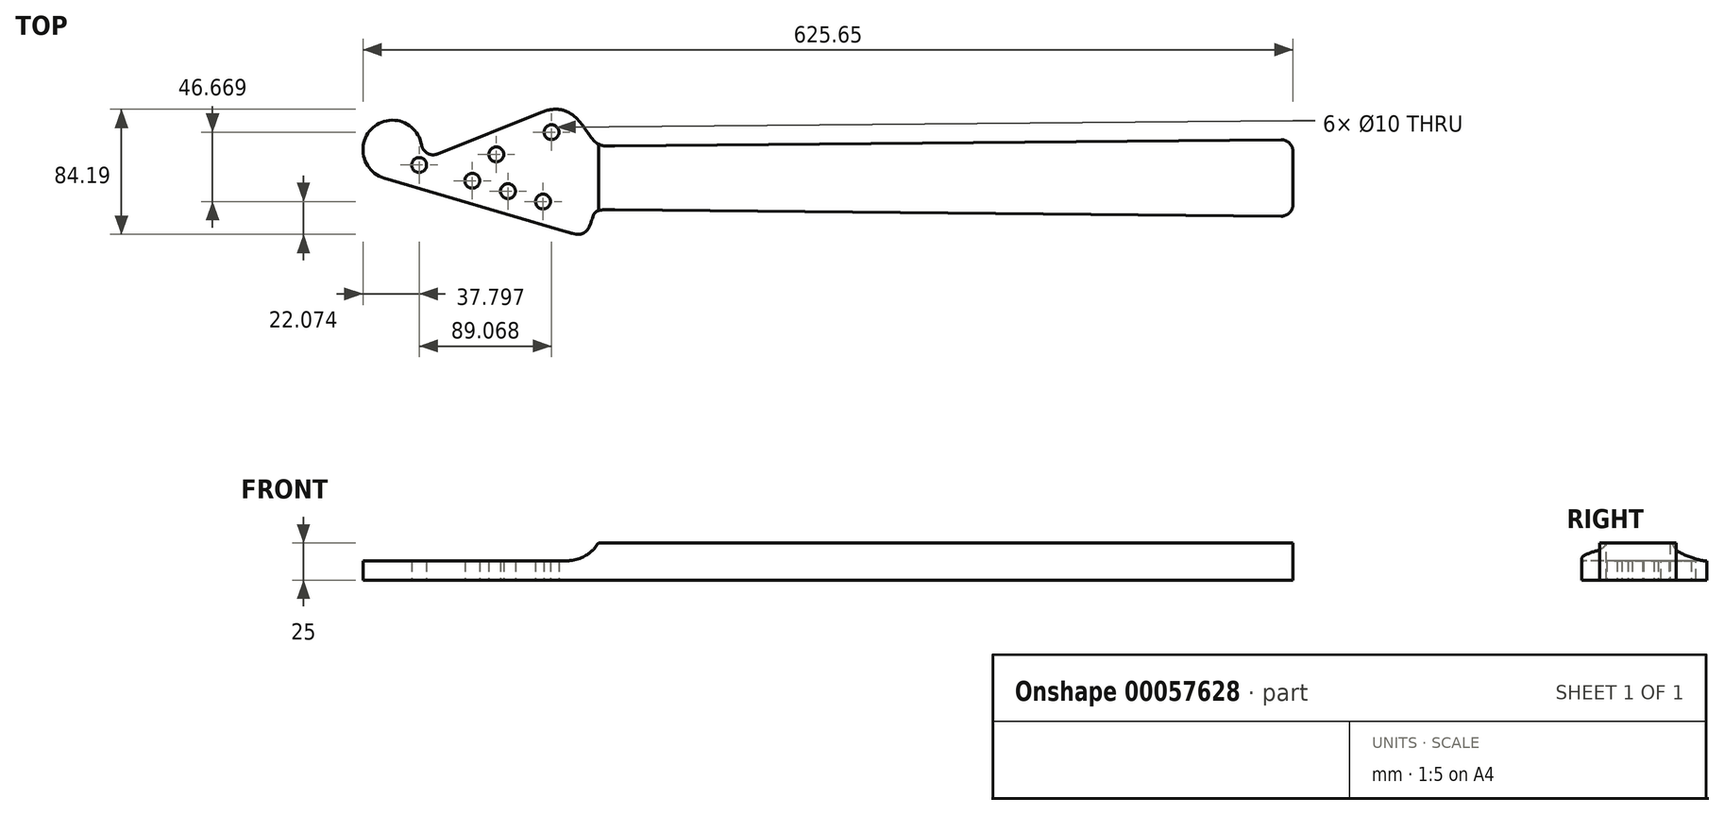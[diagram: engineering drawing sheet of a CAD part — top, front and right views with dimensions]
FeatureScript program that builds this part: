
annotation { "Feature Type Name" : "Feature", "Feature Type Description" : "" }
export const myFeature = defineFeature(function(context is Context, id is Id, definition is map)
    precondition{}
    {
        {
            var Q0;
            Q0=qCreatedBy(makeId("Top.planeOp"),FACE);
            var sketch = newSketch(context, id + "F0", { "sketchPlane" : qUnion([Q0])});
            skLineSegment(sketch, "E0", {"start": v(-545.56, 0) * mm, "end": v(270.45, 0) * mm, "construction": true});
            skLineSegment(sketch, "E1", {"start": v(-514.65, 21.5) * mm, "end": v(-514.65, -21.5) * mm, "construction": true});
            skText(sketch, "E2", { "text": "Nut", "fontName": "OpenSans-Regular.ttf"});
            skLineSegment(sketch, "E3", {"start": v(120.35, 27.5) * mm, "end": v(120.35, -27.5) * mm, "construction": true});
            skText(sketch, "E4", { "text": "Bridge\n", "fontName": "OpenSans-Regular.ttf"});
            skLineSegment(sketch, "E5", {"start": v(-514.65, 21.5) * mm, "end": v(120.35, 27.5) * mm, "construction": true});
            skLineSegment(sketch, "E6", {"start": v(-514.65, -21.5) * mm, "end": v(120.35, -27.5) * mm, "construction": true});
            skLineSegment(sketch, "E7", {"start": v(-514.65, 0) * mm, "end": v(120.35, 0) * mm});
            const initialGuessF0  = {"E2": [-0.53875, 0.11756, 1, 0, 0.01067], "E4": [0.1311, 0.11455, 1, 0, 0.02259]};
            skSetInitialGuess(sketch, initialGuessF0);
            skSolve(sketch);
        }
        {
            var Q0;
            Q0=qCreatedBy(makeId("Top.planeOp"),FACE);
            var sketch = newSketch(context, id + "F1", { "sketchPlane" : qUnion([Q0])});
            skLineSegment(sketch, "E8", {"start": v(-514.65, 21.5) * mm, "end": v(-514.65, -21.5) * mm});
            skSolve(sketch);
        }
        {
            var Q0;
            Q0=qCreatedBy(makeId("Top.planeOp"),FACE);
            var sketch = newSketch(context, id + "F2", { "sketchPlane" : qUnion([Q0])});
            skLineSegment(sketch, "E9", {"start": v(-479, 35.64) * mm, "end": v(-479, 0) * mm});
            skLineSegment(sketch, "E10", {"start": v(-514.65, 37.76) * mm, "end": v(120.35, 0) * mm, "construction": true});
            skLineSegment(sketch, "E11", {"start": v(120.35, 0) * mm, "end": v(-514.65, -21.5) * mm, "construction": true});
            skLineSegment(sketch, "E12", {"start": v(-514.65, 0) * mm, "end": v(-514.65, 37.76) * mm});
            skLineSegment(sketch, "E13", {"start": v(-514.65, 0) * mm, "end": v(-479, 0) * mm});
            skLineSegment(sketch, "E14", {"start": v(-445.37, 33.64) * mm, "end": v(-445.37, 0) * mm});
            skLineSegment(sketch, "E15", {"start": v(-445.37, 0) * mm, "end": v(-479, 0) * mm});
            skLineSegment(sketch, "E16", {"start": v(-445.37, 0) * mm, "end": v(-413.62, 0) * mm});
            skLineSegment(sketch, "E17", {"start": v(-413.62, 0) * mm, "end": v(-413.62, 31.75) * mm});
            skLineSegment(sketch, "E18", {"start": v(-413.62, 0) * mm, "end": v(-383.65, 0) * mm});
            skLineSegment(sketch, "E19", {"start": v(-383.65, 0) * mm, "end": v(-383.65, 29.97) * mm});
            skLineSegment(sketch, "E20", {"start": v(-383.65, 0) * mm, "end": v(-355.36, 0) * mm});
            skLineSegment(sketch, "E21", {"start": v(-355.36, 0) * mm, "end": v(-355.36, 28.29) * mm});
            skLineSegment(sketch, "E22", {"start": v(-355.36, 0) * mm, "end": v(-328.66, 0) * mm});
            skLineSegment(sketch, "E23", {"start": v(-328.66, 0) * mm, "end": v(-328.66, 26.7) * mm});
            skLineSegment(sketch, "E24", {"start": v(-328.66, 0) * mm, "end": v(-303.46, 0) * mm});
            skLineSegment(sketch, "E25", {"start": v(-303.46, 0) * mm, "end": v(-303.46, 25.2) * mm});
            skLineSegment(sketch, "E26", {"start": v(-303.46, 0) * mm, "end": v(-279.67, 0) * mm});
            skLineSegment(sketch, "E27", {"start": v(-279.67, 0) * mm, "end": v(-279.67, 23.79) * mm});
            skLineSegment(sketch, "E28", {"start": v(-279.67, 0) * mm, "end": v(-257.22, 0) * mm});
            skLineSegment(sketch, "E29", {"start": v(-257.22, 0) * mm, "end": v(-257.22, 22.45) * mm});
            skLineSegment(sketch, "E30", {"start": v(-257.22, 0) * mm, "end": v(-236.03, 0) * mm});
            skLineSegment(sketch, "E31", {"start": v(-236.03, 0) * mm, "end": v(-236.03, 21.2) * mm});
            skLineSegment(sketch, "E32", {"start": v(-236.03, 0) * mm, "end": v(-216.03, 0) * mm});
            skPoint(sketch, "E32.endSnap0", {"position": v(-246.63, 0) * mm});
            skLineSegment(sketch, "E33", {"start": v(-216.03, 0) * mm, "end": v(-216.03, 20) * mm});
            skLineSegment(sketch, "E34", {"start": v(-216.03, 0) * mm, "end": v(-197.15, 0) * mm});
            skLineSegment(sketch, "E35", {"start": v(-197.15, 0) * mm, "end": v(-197.15, 18.88) * mm});
            skLineSegment(sketch, "E36", {"start": v(-197.15, 0) * mm, "end": v(-179.33, 0) * mm});
            skLineSegment(sketch, "E37", {"start": v(-179.33, 0) * mm, "end": v(-179.33, 17.82) * mm});
            skLineSegment(sketch, "E38", {"start": v(-179.33, 0) * mm, "end": v(-162.5, 0) * mm});
            skLineSegment(sketch, "E39", {"start": v(-162.5, 0) * mm, "end": v(-162.5, 16.82) * mm});
            skLineSegment(sketch, "E40", {"start": v(-162.5, 0) * mm, "end": v(-146.63, 0) * mm});
            skLineSegment(sketch, "E41", {"start": v(-146.63, 0) * mm, "end": v(-146.63, 15.88) * mm});
            skLineSegment(sketch, "E42", {"start": v(-146.63, 0) * mm, "end": v(-131.65, 0) * mm});
            skLineSegment(sketch, "E43", {"start": v(-131.65, 0) * mm, "end": v(-131.65, 14.98) * mm});
            skLineSegment(sketch, "E44", {"start": v(-131.65, 0) * mm, "end": v(-117.5, 0) * mm});
            skLineSegment(sketch, "E45", {"start": v(-117.5, 0) * mm, "end": v(-117.5, 14.14) * mm});
            skLineSegment(sketch, "E46", {"start": v(-117.5, 0) * mm, "end": v(-104.16, 0) * mm});
            skLineSegment(sketch, "E47", {"start": v(-104.16, 0) * mm, "end": v(-104.16, 13.35) * mm});
            skLineSegment(sketch, "E48", {"start": v(-104.16, 0) * mm, "end": v(-91.56, 0) * mm});
            skLineSegment(sketch, "E49", {"start": v(-91.56, 0) * mm, "end": v(-91.56, 12.6) * mm});
            skLineSegment(sketch, "E50", {"start": v(-91.56, 0) * mm, "end": v(-79.66, 0) * mm});
            skLineSegment(sketch, "E51", {"start": v(-79.66, 0) * mm, "end": v(-79.66, 11.9) * mm});
            skLineSegment(sketch, "E52", {"start": v(-79.66, 0) * mm, "end": v(-68.44, 0) * mm});
            skLineSegment(sketch, "E53", {"start": v(-68.44, 0) * mm, "end": v(-68.44, 11.23) * mm});
            skSolve(sketch);
        }
        {
            var Q0;
            Q0=qCreatedBy(makeId("Top.planeOp"),FACE);
            var sketch = newSketch(context, id + "F3", { "sketchPlane" : qUnion([Q0])});
            skLineSegment(sketch, "E54", {"start": v(-514.65, 21.5) * mm, "end": v(-514.65, -21.5) * mm});
            skLineSegment(sketch, "E55", {"start": v(-514.65, -21.5) * mm, "end": v(-66.51, -25.73) * mm});
            skLineSegment(sketch, "E56", {"start": v(-58.44, -17.73) * mm, "end": v(-58.44, 17.73) * mm});
            skLineSegment(sketch, "E57", {"start": v(-66.51, 25.73) * mm, "end": v(-514.65, 21.5) * mm});
            skLineSegment(sketch, "E58", {"start": v(-68.44, 0) * mm, "end": v(-58.44, 0) * mm});
            skPoint(sketch, "E59.visualSharp", {"position": v(-58.44, -25.81) * mm});
            skArc(sketch, "E59.filletArc", {"start": v(-66.51, -25.73) * mm, "mid": v(-60.8, -23.42) * mm, "end": v(-58.44, -17.73) * mm});
            skPoint(sketch, "E60.visualSharp", {"position": v(-58.44, 25.81) * mm});
            skArc(sketch, "E60.filletArc", {"start": v(-58.44, 17.73) * mm, "mid": v(-60.8, 23.42) * mm, "end": v(-66.51, 25.73) * mm});
            skSolve(sketch);
        }
        {
            var Q0;
            Q0 = qSketchRegion(id + "F3", true);
            extrude(context, id + "F4", {"entities" : qUnion([Q0]), "depth" : 6 * mm});
        }
        {
            var Q0;
            Q0=makeQuery(id+"F4.opExtrude","CAP_FACE",FACE,{"disambiguationData":[OSD([sQuery(id+"F3.wireOp",EDGE,"E54"),sQuery(id+"F3.wireOp",EDGE,"E55"),sQuery(id+"F3.wireOp",EDGE,"E56"),sQuery(id+"F3.wireOp",EDGE,"E57")])],"isStart":false});
            cPlane(context, id + "F5", {"entities" : qUnion([Q0]), "cplaneType" : CPlaneType.OFFSET, "offset" : 0 * mm, "width" : 150 * mm, "height" : 150 * mm});
        }
        {
            var Q0;
            Q0=qCreatedBy(id+"F5.planeOp",FACE);
            var sketch = newSketch(context, id + "F6", { "sketchPlane" : qUnion([Q0])});
            skCircle(sketch, "E61", {"center": v(-429.5, 0) * mm, "radius": 3 * mm});
            skCircle(sketch, "E62", {"center": v(-369.5, 0) * mm, "radius": 3 * mm});
            skCircle(sketch, "E63", {"center": v(-316.06, 0) * mm, "radius": 3 * mm});
            skCircle(sketch, "E64", {"center": v(-268.45, 0) * mm, "radius": 3 * mm});
            skCircle(sketch, "E65", {"center": v(-226.03, 12.11) * mm, "radius": 3 * mm});
            skCircle(sketch, "E66", {"center": v(-226.03, -12.11) * mm, "radius": 3 * mm});
            skLineSegment(sketch, "E67", {"start": v(-226.03, 0) * mm, "end": v(-226.03, 12.11) * mm, "construction": true});
            skCircle(sketch, "E68", {"center": v(-170.92, 0) * mm, "radius": 3 * mm});
            skCircle(sketch, "E69", {"center": v(-139.14, 0) * mm, "radius": 3 * mm});
            skCircle(sketch, "E70", {"center": v(-110.83, 0) * mm, "radius": 3 * mm});
            skCircle(sketch, "E71", {"center": v(-85.6, 0) * mm, "radius": 3 * mm});
            skLineSegment(sketch, "E72.0", {"start": v(-514.65, 21.5) * mm, "end": v(120.35, 27.5) * mm});
            skLineSegment(sketch, "E73", {"start": v(-226.03, 0) * mm, "end": v(-226.03, 24.23) * mm, "construction": true});
            skSolve(sketch);
        }
        {
            var Q0;
            Q0 = qSketchRegion(id + "F6", true);
            var Q1;
            Q1=makeQuery(id+"F4.opExtrude","CAP_FACE",FACE,{"disambiguationData":[OSD([sQuery(id+"F3.wireOp",EDGE,"E54"),sQuery(id+"F3.wireOp",EDGE,"E55"),sQuery(id+"F3.wireOp",EDGE,"E56"),sQuery(id+"F3.wireOp",EDGE,"E57")])],"isStart":true});
            extrude(context, id + "F7", {"entities" : qUnion([Q0]), "operationType" : NewBodyOperationType.REMOVE, "oppositeDirection" : true, "endBoundEntityFace" : qUnion([Q1]), "depth" : 2 * mm});
        }
        {
            var Q0;
            Q0=makeQuery(id+"F4.opExtrude","SWEPT_FACE",FACE,{"disambiguationData":[OSD([sQuery(id+"F3.wireOp",EDGE,"E56")])]});
            var sketch = newSketch(context, id + "F8", { "sketchPlane" : qUnion([Q0])});
            skArc(sketch, "E74", {"start": v(53.48, 0) * mm, "mid": v(0, 6) * mm, "end": v(-53.48, 0) * mm});
            skLineSegment(sketch, "E75", {"start": v(-53.48, 0) * mm, "end": v(-53.48, 6) * mm});
            skLineSegment(sketch, "E76", {"start": v(-53.48, 6) * mm, "end": v(53.48, 6) * mm});
            skLineSegment(sketch, "E77", {"start": v(53.48, 6) * mm, "end": v(53.48, 0) * mm});
            skSolve(sketch);
        }
        {
            var Q0;
            Q0 = qSketchRegion(id + "F8", true);
            extrude(context, id + "F9", {"entities" : qUnion([Q0]), "operationType" : NewBodyOperationType.REMOVE, "endBound" : BoundingType.THROUGH_ALL, "oppositeDirection" : true, "depth" : 25 * mm});
        }
        {
            var Q0;
            Q0=qCreatedBy(id+"F5.planeOp",FACE);
            var sketch = newSketch(context, id + "F10", { "sketchPlane" : qUnion([Q0])});
            skLineSegment(sketch, "E78.0", {"start": v(-514.65, 21.5) * mm, "end": v(-514.65, -21.5) * mm});
            skLineSegment(sketch, "E79.0", {"start": v(-58.44, 25.76) * mm, "end": v(-58.44, -25.76) * mm});
            skLineSegment(sketch, "E80", {"start": v(-514.65, 18.5) * mm, "end": v(-58.44, 22.81) * mm, "construction": true});
            skLineSegment(sketch, "E81", {"start": v(-514.65, -18.5) * mm, "end": v(-58.44, -22.81) * mm, "construction": true});
            skLineSegment(sketch, "E82", {"start": v(-479, 18.84) * mm, "end": v(-479, -18.84) * mm});
            skLineSegment(sketch, "E83", {"start": v(-445.37, 19.15) * mm, "end": v(-445.37, -19.15) * mm});
            skArc(sketch, "E84.0.startCap", {"start": v(-479.3, 18.84) * mm, "mid": v(-479, 19.14) * mm, "end": v(-478.7, 18.84) * mm});
            skArc(sketch, "E84.0.endCap", {"start": v(-478.7, -18.84) * mm, "mid": v(-479, -19.14) * mm, "end": v(-479.3, -18.84) * mm});
            skLineSegment(sketch, "E84.0.left", {"start": v(-478.7, 18.84) * mm, "end": v(-478.7, -18.84) * mm});
            skLineSegment(sketch, "E84.0.right", {"start": v(-479.3, 18.84) * mm, "end": v(-479.3, -18.84) * mm});
            skArc(sketch, "E85.0.startCap", {"start": v(-445.67, 19.15) * mm, "mid": v(-445.37, 19.45) * mm, "end": v(-445.07, 19.15) * mm});
            skArc(sketch, "E85.0.endCap", {"start": v(-445.07, -19.15) * mm, "mid": v(-445.37, -19.45) * mm, "end": v(-445.67, -19.15) * mm});
            skLineSegment(sketch, "E85.0.left", {"start": v(-445.07, 19.15) * mm, "end": v(-445.07, -19.15) * mm});
            skLineSegment(sketch, "E85.0.right", {"start": v(-445.67, 19.15) * mm, "end": v(-445.67, -19.15) * mm});
            skLineSegment(sketch, "E86", {"start": v(-413.62, 19.45) * mm, "end": v(-413.62, -19.45) * mm});
            skLineSegment(sketch, "E87", {"start": v(-383.65, 19.74) * mm, "end": v(-383.65, -19.74) * mm});
            skArc(sketch, "E88.0.startCap", {"start": v(-413.92, 19.45) * mm, "mid": v(-413.62, 19.75) * mm, "end": v(-413.32, 19.45) * mm});
            skArc(sketch, "E88.0.endCap", {"start": v(-413.32, -19.45) * mm, "mid": v(-413.62, -19.75) * mm, "end": v(-413.92, -19.45) * mm});
            skLineSegment(sketch, "E88.0.left", {"start": v(-413.32, 19.45) * mm, "end": v(-413.32, -19.45) * mm});
            skLineSegment(sketch, "E88.0.right", {"start": v(-413.92, 19.45) * mm, "end": v(-413.92, -19.45) * mm});
            skArc(sketch, "E89.0.startCap", {"start": v(-383.95, 19.74) * mm, "mid": v(-383.65, 20.04) * mm, "end": v(-383.35, 19.74) * mm});
            skArc(sketch, "E89.0.endCap", {"start": v(-383.35, -19.74) * mm, "mid": v(-383.65, -20.04) * mm, "end": v(-383.95, -19.74) * mm});
            skLineSegment(sketch, "E89.0.left", {"start": v(-383.35, 19.74) * mm, "end": v(-383.35, -19.74) * mm});
            skLineSegment(sketch, "E89.0.right", {"start": v(-383.95, 19.74) * mm, "end": v(-383.95, -19.74) * mm});
            skLineSegment(sketch, "E90", {"start": v(-355.36, -20) * mm, "end": v(-355.36, 20) * mm});
            skArc(sketch, "E91.0.startCap", {"start": v(-355.06, -20) * mm, "mid": v(-355.36, -20.3) * mm, "end": v(-355.66, -20) * mm});
            skArc(sketch, "E91.0.endCap", {"start": v(-355.66, 20) * mm, "mid": v(-355.36, 20.3) * mm, "end": v(-355.06, 20) * mm});
            skLineSegment(sketch, "E91.0.left", {"start": v(-355.66, -20) * mm, "end": v(-355.66, 20) * mm});
            skLineSegment(sketch, "E91.0.right", {"start": v(-355.06, -20) * mm, "end": v(-355.06, 20) * mm});
            skLineSegment(sketch, "E92", {"start": v(-328.66, -20.26) * mm, "end": v(-328.66, 20.26) * mm});
            skArc(sketch, "E93.0.startCap", {"start": v(-328.36, -20.26) * mm, "mid": v(-328.66, -20.56) * mm, "end": v(-328.96, -20.26) * mm});
            skArc(sketch, "E93.0.endCap", {"start": v(-328.96, 20.26) * mm, "mid": v(-328.66, 20.56) * mm, "end": v(-328.36, 20.26) * mm});
            skLineSegment(sketch, "E93.0.left", {"start": v(-328.96, -20.26) * mm, "end": v(-328.96, 20.26) * mm});
            skLineSegment(sketch, "E93.0.right", {"start": v(-328.36, -20.26) * mm, "end": v(-328.36, 20.26) * mm});
            skLineSegment(sketch, "E94", {"start": v(-303.46, 20.5) * mm, "end": v(-303.46, -20.5) * mm});
            skArc(sketch, "E95.0.startCap", {"start": v(-303.76, 20.5) * mm, "mid": v(-303.46, 20.8) * mm, "end": v(-303.16, 20.5) * mm});
            skArc(sketch, "E95.0.endCap", {"start": v(-303.16, -20.5) * mm, "mid": v(-303.46, -20.8) * mm, "end": v(-303.76, -20.5) * mm});
            skLineSegment(sketch, "E95.0.left", {"start": v(-303.16, 20.5) * mm, "end": v(-303.16, -20.5) * mm});
            skLineSegment(sketch, "E95.0.right", {"start": v(-303.76, 20.5) * mm, "end": v(-303.76, -20.5) * mm});
            skLineSegment(sketch, "E96", {"start": v(-279.67, 20.72) * mm, "end": v(-279.67, -20.72) * mm});
            skArc(sketch, "E97.0.startCap", {"start": v(-279.97, 20.72) * mm, "mid": v(-279.67, 21.02) * mm, "end": v(-279.37, 20.72) * mm});
            skArc(sketch, "E97.0.endCap", {"start": v(-279.37, -20.72) * mm, "mid": v(-279.67, -21.02) * mm, "end": v(-279.97, -20.72) * mm});
            skLineSegment(sketch, "E97.0.left", {"start": v(-279.37, 20.72) * mm, "end": v(-279.37, -20.72) * mm});
            skLineSegment(sketch, "E97.0.right", {"start": v(-279.97, 20.72) * mm, "end": v(-279.97, -20.72) * mm});
            skLineSegment(sketch, "E98", {"start": v(-257.22, -20.93) * mm, "end": v(-257.22, 20.93) * mm});
            skArc(sketch, "E99.0.startCap", {"start": v(-256.92, -20.93) * mm, "mid": v(-257.22, -21.23) * mm, "end": v(-257.52, -20.93) * mm});
            skArc(sketch, "E99.0.endCap", {"start": v(-257.52, 20.93) * mm, "mid": v(-257.22, 21.23) * mm, "end": v(-256.92, 20.93) * mm});
            skLineSegment(sketch, "E99.0.left", {"start": v(-257.52, -20.93) * mm, "end": v(-257.52, 20.93) * mm});
            skLineSegment(sketch, "E99.0.right", {"start": v(-256.92, -20.93) * mm, "end": v(-256.92, 20.93) * mm});
            skLineSegment(sketch, "E100", {"start": v(-236.03, 21.13) * mm, "end": v(-236.03, -21.13) * mm});
            skArc(sketch, "E101.0.startCap", {"start": v(-236.33, 21.13) * mm, "mid": v(-236.03, 21.43) * mm, "end": v(-235.73, 21.13) * mm});
            skArc(sketch, "E101.0.endCap", {"start": v(-235.73, -21.13) * mm, "mid": v(-236.03, -21.43) * mm, "end": v(-236.33, -21.13) * mm});
            skLineSegment(sketch, "E101.0.left", {"start": v(-235.73, 21.13) * mm, "end": v(-235.73, -21.13) * mm});
            skLineSegment(sketch, "E101.0.right", {"start": v(-236.33, 21.13) * mm, "end": v(-236.33, -21.13) * mm});
            skLineSegment(sketch, "E102", {"start": v(-216.03, 21.32) * mm, "end": v(-216.03, -21.32) * mm});
            skArc(sketch, "E103.0.startCap", {"start": v(-216.33, 21.32) * mm, "mid": v(-216.03, 21.62) * mm, "end": v(-215.73, 21.32) * mm});
            skArc(sketch, "E103.0.endCap", {"start": v(-215.73, -21.32) * mm, "mid": v(-216.03, -21.62) * mm, "end": v(-216.33, -21.32) * mm});
            skLineSegment(sketch, "E103.0.left", {"start": v(-215.73, 21.32) * mm, "end": v(-215.73, -21.32) * mm});
            skLineSegment(sketch, "E103.0.right", {"start": v(-216.33, 21.32) * mm, "end": v(-216.33, -21.32) * mm});
            skLineSegment(sketch, "E104", {"start": v(-197.15, 21.5) * mm, "end": v(-197.15, -21.5) * mm});
            skArc(sketch, "E105.0.startCap", {"start": v(-197.45, 21.5) * mm, "mid": v(-197.15, 21.8) * mm, "end": v(-196.85, 21.5) * mm});
            skArc(sketch, "E105.0.endCap", {"start": v(-196.85, -21.5) * mm, "mid": v(-197.15, -21.8) * mm, "end": v(-197.45, -21.5) * mm});
            skLineSegment(sketch, "E105.0.left", {"start": v(-196.85, 21.5) * mm, "end": v(-196.85, -21.5) * mm});
            skLineSegment(sketch, "E105.0.right", {"start": v(-197.45, 21.5) * mm, "end": v(-197.45, -21.5) * mm});
            skLineSegment(sketch, "E106", {"start": v(-179.33, 21.67) * mm, "end": v(-179.33, -21.67) * mm});
            skArc(sketch, "E107.0.startCap", {"start": v(-179.63, 21.67) * mm, "mid": v(-179.33, 21.97) * mm, "end": v(-179.03, 21.67) * mm});
            skArc(sketch, "E107.0.endCap", {"start": v(-179.03, -21.67) * mm, "mid": v(-179.33, -21.97) * mm, "end": v(-179.63, -21.67) * mm});
            skLineSegment(sketch, "E107.0.left", {"start": v(-179.03, 21.67) * mm, "end": v(-179.03, -21.67) * mm});
            skLineSegment(sketch, "E107.0.right", {"start": v(-179.63, 21.67) * mm, "end": v(-179.63, -21.67) * mm});
            skLineSegment(sketch, "E108", {"start": v(-162.5, 21.83) * mm, "end": v(-162.5, -21.83) * mm});
            skArc(sketch, "E109.0.startCap", {"start": v(-162.8, 21.83) * mm, "mid": v(-162.5, 22.13) * mm, "end": v(-162.2, 21.83) * mm});
            skArc(sketch, "E109.0.endCap", {"start": v(-162.2, -21.83) * mm, "mid": v(-162.5, -22.13) * mm, "end": v(-162.8, -21.83) * mm});
            skLineSegment(sketch, "E109.0.left", {"start": v(-162.2, 21.83) * mm, "end": v(-162.2, -21.83) * mm});
            skLineSegment(sketch, "E109.0.right", {"start": v(-162.8, 21.83) * mm, "end": v(-162.8, -21.83) * mm});
            skLineSegment(sketch, "E110", {"start": v(-146.63, 21.98) * mm, "end": v(-146.63, -21.98) * mm});
            skArc(sketch, "E111.0.startCap", {"start": v(-146.93, 21.98) * mm, "mid": v(-146.63, 22.28) * mm, "end": v(-146.33, 21.98) * mm});
            skArc(sketch, "E111.0.endCap", {"start": v(-146.33, -21.98) * mm, "mid": v(-146.63, -22.28) * mm, "end": v(-146.93, -21.98) * mm});
            skLineSegment(sketch, "E111.0.left", {"start": v(-146.33, 21.98) * mm, "end": v(-146.33, -21.98) * mm});
            skLineSegment(sketch, "E111.0.right", {"start": v(-146.93, 21.98) * mm, "end": v(-146.93, -21.98) * mm});
            skLineSegment(sketch, "E112", {"start": v(-131.65, 22.12) * mm, "end": v(-131.65, -22.12) * mm});
            skArc(sketch, "E113.0.startCap", {"start": v(-131.95, 22.12) * mm, "mid": v(-131.65, 22.42) * mm, "end": v(-131.35, 22.12) * mm});
            skArc(sketch, "E113.0.endCap", {"start": v(-131.35, -22.12) * mm, "mid": v(-131.65, -22.42) * mm, "end": v(-131.95, -22.12) * mm});
            skLineSegment(sketch, "E113.0.left", {"start": v(-131.35, 22.12) * mm, "end": v(-131.35, -22.12) * mm});
            skLineSegment(sketch, "E113.0.right", {"start": v(-131.95, 22.12) * mm, "end": v(-131.95, -22.12) * mm});
            skLineSegment(sketch, "E114", {"start": v(-117.5, 22.25) * mm, "end": v(-117.5, -22.25) * mm});
            skArc(sketch, "E115.0.startCap", {"start": v(-117.8, 22.25) * mm, "mid": v(-117.5, 22.55) * mm, "end": v(-117.2, 22.25) * mm});
            skArc(sketch, "E115.0.endCap", {"start": v(-117.2, -22.25) * mm, "mid": v(-117.5, -22.55) * mm, "end": v(-117.8, -22.25) * mm});
            skLineSegment(sketch, "E115.0.left", {"start": v(-117.2, 22.25) * mm, "end": v(-117.2, -22.25) * mm});
            skLineSegment(sketch, "E115.0.right", {"start": v(-117.8, 22.25) * mm, "end": v(-117.8, -22.25) * mm});
            skLineSegment(sketch, "E116", {"start": v(-104.16, 22.38) * mm, "end": v(-104.16, -22.38) * mm});
            skArc(sketch, "E117.0.startCap", {"start": v(-104.46, 22.38) * mm, "mid": v(-104.16, 22.68) * mm, "end": v(-103.86, 22.38) * mm});
            skArc(sketch, "E117.0.endCap", {"start": v(-103.86, -22.38) * mm, "mid": v(-104.16, -22.68) * mm, "end": v(-104.46, -22.38) * mm});
            skLineSegment(sketch, "E117.0.left", {"start": v(-103.86, 22.38) * mm, "end": v(-103.86, -22.38) * mm});
            skLineSegment(sketch, "E117.0.right", {"start": v(-104.46, 22.38) * mm, "end": v(-104.46, -22.38) * mm});
            skLineSegment(sketch, "E118", {"start": v(-91.56, 22.5) * mm, "end": v(-91.56, -22.5) * mm});
            skArc(sketch, "E119.0.startCap", {"start": v(-91.86, 22.5) * mm, "mid": v(-91.56, 22.8) * mm, "end": v(-91.26, 22.5) * mm});
            skArc(sketch, "E119.0.endCap", {"start": v(-91.26, -22.5) * mm, "mid": v(-91.56, -22.8) * mm, "end": v(-91.86, -22.5) * mm});
            skLineSegment(sketch, "E119.0.left", {"start": v(-91.26, 22.5) * mm, "end": v(-91.26, -22.5) * mm});
            skLineSegment(sketch, "E119.0.right", {"start": v(-91.86, 22.5) * mm, "end": v(-91.86, -22.5) * mm});
            skLineSegment(sketch, "E120", {"start": v(-79.66, -22.61) * mm, "end": v(-79.66, 22.61) * mm});
            skArc(sketch, "E121.0.startCap", {"start": v(-79.36, -22.61) * mm, "mid": v(-79.66, -22.91) * mm, "end": v(-79.96, -22.61) * mm});
            skArc(sketch, "E121.0.endCap", {"start": v(-79.96, 22.61) * mm, "mid": v(-79.66, 22.91) * mm, "end": v(-79.36, 22.61) * mm});
            skLineSegment(sketch, "E121.0.left", {"start": v(-79.96, -22.61) * mm, "end": v(-79.96, 22.61) * mm});
            skLineSegment(sketch, "E121.0.right", {"start": v(-79.36, -22.61) * mm, "end": v(-79.36, 22.61) * mm});
            skLineSegment(sketch, "E122", {"start": v(-68.44, 22.72) * mm, "end": v(-68.44, -22.72) * mm});
            skArc(sketch, "E123.0.startCap", {"start": v(-68.74, 22.72) * mm, "mid": v(-68.44, 23.02) * mm, "end": v(-68.14, 22.72) * mm});
            skArc(sketch, "E123.0.endCap", {"start": v(-68.14, -22.72) * mm, "mid": v(-68.44, -23.02) * mm, "end": v(-68.74, -22.72) * mm});
            skLineSegment(sketch, "E123.0.left", {"start": v(-68.14, 22.72) * mm, "end": v(-68.14, -22.72) * mm});
            skLineSegment(sketch, "E123.0.right", {"start": v(-68.74, 22.72) * mm, "end": v(-68.74, -22.72) * mm});
            skSolve(sketch);
        }
        {
            var Q0;
            Q0 = qSketchRegion(id + "F10", true);
            extrude(context, id + "F11", {"entities" : qUnion([Q0]), "operationType" : NewBodyOperationType.REMOVE, "oppositeDirection" : true, "depth" : 4 * mm});
        }
        {
            var Q0;
            Q0=makeQuery(id+"F4.opExtrude","SWEPT_FACE",FACE,{"disambiguationData":[OSD([sQuery(id+"F3.wireOp",EDGE,"E55")])]});
            var sketch = newSketch(context, id + "F12", { "sketchPlane" : qUnion([Q0])});
            skPoint(sketch, "E124.0", {"position": v(-429.48, 6) * mm});
            skLineSegment(sketch, "E125", {"start": v(-429.48, 6) * mm, "end": v(-429.48, 0) * mm, "construction": true});
            skCircle(sketch, "E126", {"center": v(-429.48, 2) * mm, "radius": 1 * mm});
            skLineSegment(sketch, "E127", {"start": v(-298.57, 2) * mm, "end": v(-514.42, 2) * mm, "construction": true});
            skPoint(sketch, "E128.0", {"position": v(-369.49, 6) * mm});
            skLineSegment(sketch, "E129", {"start": v(-369.49, 6) * mm, "end": v(-369.49, 0) * mm, "construction": true});
            skCircle(sketch, "E130", {"center": v(-369.49, 2) * mm, "radius": 1 * mm});
            skPoint(sketch, "E131.0", {"position": v(-316.05, 6) * mm});
            skPoint(sketch, "E132.0", {"position": v(-268.44, 6) * mm});
            skPoint(sketch, "E133.0", {"position": v(-225.9, 6) * mm});
            skPoint(sketch, "E134.0", {"position": v(-170.91, 6) * mm});
            skPoint(sketch, "E135.0", {"position": v(-139.14, 6) * mm});
            skPoint(sketch, "E136.0", {"position": v(-110.83, 6) * mm});
            skPoint(sketch, "E137.0", {"position": v(-85.6, 6) * mm});
            skLineSegment(sketch, "E138", {"start": v(-85.6, 6) * mm, "end": v(-85.6, 0) * mm, "construction": true});
            skLineSegment(sketch, "E139", {"start": v(-110.83, 6) * mm, "end": v(-110.83, 0) * mm, "construction": true});
            skLineSegment(sketch, "E140", {"start": v(-139.14, 6) * mm, "end": v(-139.14, 0) * mm, "construction": true});
            skLineSegment(sketch, "E141", {"start": v(-170.91, 6) * mm, "end": v(-170.91, 0) * mm, "construction": true});
            skLineSegment(sketch, "E142", {"start": v(-225.9, 6) * mm, "end": v(-225.9, 0) * mm, "construction": true});
            skLineSegment(sketch, "E143", {"start": v(-268.44, 6) * mm, "end": v(-268.44, 0) * mm, "construction": true});
            skLineSegment(sketch, "E144", {"start": v(-316.05, 6) * mm, "end": v(-316.05, 0) * mm, "construction": true});
            skCircle(sketch, "E145", {"center": v(-85.6, 2) * mm, "radius": 1 * mm});
            skCircle(sketch, "E146", {"center": v(-110.83, 2) * mm, "radius": 1 * mm});
            skCircle(sketch, "E147", {"center": v(-139.14, 2) * mm, "radius": 1 * mm});
            skCircle(sketch, "E148", {"center": v(-268.44, 2) * mm, "radius": 1 * mm});
            skLineSegment(sketch, "E149.0", {"start": v(-236.02, 0) * mm, "end": v(-236.22, 0) * mm});
            skLineSegment(sketch, "E150.0", {"start": v(-216.02, 0) * mm, "end": v(-216.2, 0) * mm});
            skPoint(sketch, "E151", {"position": v(-225.9, 2) * mm});
            skCircle(sketch, "E152", {"center": v(-316.05, 2) * mm, "radius": 1 * mm});
            skLineSegment(sketch, "E153", {"start": v(-216.02, 0) * mm, "end": v(-216.02, 4.13) * mm});
            skPoint(sketch, "E154", {"position": v(-216.02, 2) * mm});
            skCircle(sketch, "E155", {"center": v(-220.96, 2) * mm, "radius": 1 * mm});
            skCircle(sketch, "E156", {"center": v(-170.91, 2) * mm, "radius": 1 * mm});
            skCircle(sketch, "E157", {"center": v(-230.85, 2) * mm, "radius": 1 * mm});
            skSolve(sketch);
        }
        {
            var Q0;
            Q0 = qSketchRegion(id + "F12", true);
            extrude(context, id + "F13", {"entities" : qUnion([Q0]), "operationType" : NewBodyOperationType.REMOVE, "oppositeDirection" : true, "depth" : 2 * mm});
        }
        {
            var Q0;
            Q0=qCreatedBy(makeId("Top.planeOp"),FACE);
            var sketch = newSketch(context, id + "F14", { "sketchPlane" : qUnion([Q0])});
            skLineSegment(sketch, "E158", {"start": v(-58.44, 70.43) * mm, "end": v(-58.44, -45.52) * mm});
            skLineSegment(sketch, "E159", {"start": v(-58.44, -45.52) * mm, "end": v(-731.05, -45.52) * mm});
            skLineSegment(sketch, "E160", {"start": v(-731.05, -45.52) * mm, "end": v(-731.05, 70.43) * mm});
            skLineSegment(sketch, "E161", {"start": v(-731.05, 70.43) * mm, "end": v(-58.44, 70.43) * mm});
            skSolve(sketch);
        }
        {
            var Q0;
            Q0=makeQuery(id+"F14.imprint","IMPRINT",FACE,{"disambiguationData":[TD([[makeQuery(id+"F14.imprint","IMPRINT",EDGE,{"derivedFrom":sQuery(id+"F14.wireOp",EDGE,"E158")}),-1.0]])]});
            extrude(context, id + "F15", {"entities" : qUnion([Q0]), "oppositeDirection" : true, "depth" : 25 * mm});
        }
        {
            var Q0;
            Q0=makeQuery(id+"F15.opExtrude","CAP_FACE",FACE,{"disambiguationData":[OSD([sQuery(id+"F14.wireOp",EDGE,"E158"),sQuery(id+"F14.wireOp",EDGE,"E159"),sQuery(id+"F14.wireOp",EDGE,"E160"),sQuery(id+"F14.wireOp",EDGE,"E161")])],"isStart":false});
            var sketch = newSketch(context, id + "F16", { "sketchPlane" : qUnion([Q0])});
            skLineSegment(sketch, "E162", {"start": v(-646.3, -8.69) * mm, "end": v(-562.92, 15.9) * mm, "construction": true});
            skLineSegment(sketch, "E163", {"start": v(-594.35, -15.84) * mm, "end": v(-557.22, -30.77) * mm, "construction": true});
            skCircle(sketch, "E164", {"center": v(-646.3, -8.69) * mm, "radius": 5 * mm});
            skCircle(sketch, "E165", {"center": v(-610.48, 1.87) * mm, "radius": 5 * mm});
            skCircle(sketch, "E166", {"center": v(-586.49, 8.95) * mm, "radius": 5 * mm});
            skCircle(sketch, "E167", {"center": v(-562.92, 15.9) * mm, "radius": 5 * mm});
            skCircle(sketch, "E168", {"center": v(-594.35, -15.84) * mm, "radius": 5 * mm});
            skCircle(sketch, "E169", {"center": v(-557.22, -30.77) * mm, "radius": 5 * mm});
            skSolve(sketch);
        }
        {
            var Q0;
            Q0 = qSketchRegion(id + "F16", true);
            extrude(context, id + "F17", {"entities" : qUnion([Q0]), "operationType" : NewBodyOperationType.REMOVE, "endBound" : BoundingType.THROUGH_ALL, "oppositeDirection" : true, "depth" : 25 * mm});
        }
        {
            var Q0;
            Q0=qCreatedBy(makeId("Top.planeOp"),FACE);
            var sketch = newSketch(context, id + "F18", { "sketchPlane" : qUnion([Q0])});
            skLineSegment(sketch, "E170.0", {"start": v(-58.44, -17.73) * mm, "end": v(-58.44, 17.73) * mm});
            skLineSegment(sketch, "E171.0", {"start": v(-66.51, 25.73) * mm, "end": v(-514.65, 21.5) * mm});
            skLineSegment(sketch, "E172", {"start": v(-514.65, -21.5) * mm, "end": v(-66.51, -25.73) * mm});
            skFitSpline(sketch, "E173", {"points": [v(-514.65, -21.5) * mm, v(-528.95, -25.07) * mm, v(-543.18, -37.36) * mm], "startDerivative": vector(-60.43, 0.57) * mm, "endDerivative": vector(-63.56, 18.74) * mm});
            skLineSegment(sketch, "E174", {"start": v(-543.18, -37.36) * mm, "end": v(-669.86, 0) * mm});
            skArc(sketch, "E175", {"start": v(-644.68, 22.26) * mm, "mid": v(-677.39, 33.89) * mm, "end": v(-669.86, 0) * mm});
            skArc(sketch, "E176", {"start": v(-644.68, 22.26) * mm, "mid": v(-640.71, 16.59) * mm, "end": v(-633.8, 16.14) * mm});
            skLineSegment(sketch, "E177", {"start": v(-633.8, 16.14) * mm, "end": v(-564.31, 44.1) * mm});
            skFitSpline(sketch, "E178", {"points": [v(-514.65, 21.5) * mm, v(-528.8, 25.14) * mm, v(-564.31, 44.1) * mm], "startDerivative": vector(-47.75, -0.45) * mm, "endDerivative": vector(-104.5, -42.03) * mm});
            skPoint(sketch, "E179.visualSharp", {"position": v(-58.44, 25.81) * mm});
            skArc(sketch, "E179.filletArc", {"start": v(-58.44, 17.73) * mm, "mid": v(-60.8, 23.42) * mm, "end": v(-66.51, 25.73) * mm});
            skPoint(sketch, "E180.visualSharp", {"position": v(-58.44, -25.81) * mm});
            skArc(sketch, "E180.filletArc", {"start": v(-66.51, -25.73) * mm, "mid": v(-60.8, -23.42) * mm, "end": v(-58.44, -17.73) * mm});
            skLineSegment(sketch, "E181.0", {"start": v(-594.35, 15.84) * mm, "end": v(-557.22, 30.77) * mm});
            skLineSegment(sketch, "E182.0", {"start": v(-646.3, 8.69) * mm, "end": v(-562.92, -15.9) * mm});
            skSolve(sketch);
        }
        {
            var Q0;
            Q0 = qSketchRegion(id + "F18", true);
            var Q1;
            Q1 = qSketchRegion(id + "F16", true);
            extrude(context, id + "F19", {"entities" : qUnion([Q0, Q1]), "operationType" : NewBodyOperationType.INTERSECT, "oppositeDirection" : true, "depth" : 25 * mm});
        }
        {
            var Q0;
            Q0=qCreatedBy(makeId("Front.planeOp"),FACE);
            var sketch = newSketch(context, id + "F20", { "sketchPlane" : qUnion([Q0])});
            skFitSpline(sketch, "E183.0", {"points": [v(-890.47, -43.26) * mm, v(-896.1, -43.26) * mm, v(-905.56, -43.26) * mm, v(-915.53, -43.26) * mm, v(-922.39, -43.26) * mm, v(-926.45, -43.26) * mm, v(-929.27, -43.26) * mm, v(-931.32, -43.26) * mm, v(-933.43, -43.26) * mm, v(-935.75, -43.26) * mm, v(-938.24, -43.26) * mm, v(-941.76, -43.26) * mm, v(-946.45, -43.26) * mm, v(-951.34, -43.26) * mm, v(-955.27, -43.26) * mm, v(-958.2, -43.26) * mm, v(-961.08, -43.26) * mm, v(-964.99, -43.26) * mm, v(-970.12, -43.26) * mm, v(-977.21, -43.26) * mm, v(-984.33, -43.26) * mm, v(-991, -43.26) * mm, v(-996.58, -43.26) * mm, v(-1002.76, -43.26) * mm, v(-1009.65, -43.26) * mm, v(-1017.15, -43.26) * mm, v(-1027.88, -43.26) * mm, v(-1042.46, -43.26) * mm, v(-1061.2, -43.26) * mm, v(-1087.01, -43.26) * mm, v(-1112.84, -43.26) * mm, v(-1136.2, -43.26) * mm, v(-1151.88, -43.26) * mm, v(-1165.08, -43.26) * mm, v(-1173.51, -43.26) * mm, v(-1178.4, -43.26) * mm, v(-1181.05, -43.26) * mm, v(-1182.65, -43.26) * mm, v(-1183.5, -43.26) * mm, v(-1182.33, -43.26) * mm, v(-1177.99, -43.26) * mm, v(-1171.32, -43.26) * mm, v(-1162.96, -43.26) * mm, v(-1155.1, -43.26) * mm, v(-1148.57, -43.26) * mm, v(-1143.63, -43.26) * mm, v(-1138.74, -43.26) * mm, v(-1133.95, -43.26) * mm, v(-1129.25, -43.26) * mm, v(-1123.1, -43.26) * mm, v(-1115.6, -43.26) * mm, v(-1103.94, -43.26) * mm, v(-1092.64, -43.26) * mm, v(-1081.48, -43.26) * mm, v(-1073.11, -43.26) * mm, v(-1064.64, -43.26) * mm, v(-1055.9, -43.26) * mm, v(-1046.79, -43.26) * mm, v(-1037.14, -43.26) * mm, v(-1028.55, -43.26) * mm, v(-1021.28, -43.26) * mm, v(-1015.6, -43.26) * mm, v(-1009.73, -43.26) * mm, v(-1001.71, -43.26) * mm, v(-991.47, -43.26) * mm, v(-979.23, -43.26) * mm, v(-967.42, -43.26) * mm, v(-956.46, -43.26) * mm, v(-948.37, -43.26) * mm, v(-942.71, -43.26) * mm, v(-938.93, -43.26) * mm, v(-935.67, -43.26) * mm, v(-932.92, -43.26) * mm, v(-930.58, -43.26) * mm, v(-927.9, -43.26) * mm, v(-925.15, -43.26) * mm, v(-922.18, -43.26) * mm, v(-918.84, -43.26) * mm, v(-914.55, -43.26) * mm, v(-906.9, -43.26) * mm, v(-898.23, -43.26) * mm, v(-890.47, -43.26) * mm, v(-890.47, -43.26) * mm]});
            skFitSpline(sketch, "E184.0", {"points": [v(-890.47, -43.26) * mm, v(-896.1, -43.26) * mm, v(-905.56, -43.26) * mm, v(-915.53, -43.26) * mm, v(-922.39, -43.26) * mm, v(-926.45, -43.26) * mm, v(-929.27, -43.26) * mm, v(-931.32, -43.26) * mm, v(-933.43, -43.26) * mm, v(-935.75, -43.26) * mm, v(-938.24, -43.26) * mm, v(-941.76, -43.26) * mm, v(-946.45, -43.26) * mm, v(-951.34, -43.26) * mm, v(-955.27, -43.26) * mm, v(-958.2, -43.26) * mm, v(-961.08, -43.26) * mm, v(-964.99, -43.26) * mm, v(-970.12, -43.26) * mm, v(-977.21, -43.26) * mm, v(-984.33, -43.26) * mm, v(-991, -43.26) * mm, v(-996.58, -43.26) * mm, v(-1002.76, -43.26) * mm, v(-1009.65, -43.26) * mm, v(-1017.15, -43.26) * mm, v(-1027.88, -43.26) * mm, v(-1042.46, -43.26) * mm, v(-1061.2, -43.26) * mm, v(-1087.01, -43.26) * mm, v(-1112.84, -43.26) * mm, v(-1136.2, -43.26) * mm, v(-1151.88, -43.26) * mm, v(-1165.08, -43.26) * mm, v(-1173.51, -43.26) * mm, v(-1178.4, -43.26) * mm, v(-1181.05, -43.26) * mm, v(-1182.65, -43.26) * mm, v(-1183.5, -43.26) * mm, v(-1182.33, -43.26) * mm, v(-1177.99, -43.26) * mm, v(-1171.32, -43.26) * mm, v(-1162.96, -43.26) * mm, v(-1155.1, -43.26) * mm, v(-1148.57, -43.26) * mm, v(-1143.63, -43.26) * mm, v(-1138.74, -43.26) * mm, v(-1133.95, -43.26) * mm, v(-1129.25, -43.26) * mm, v(-1123.1, -43.26) * mm, v(-1115.6, -43.26) * mm, v(-1103.94, -43.26) * mm, v(-1092.64, -43.26) * mm, v(-1081.48, -43.26) * mm, v(-1073.11, -43.26) * mm, v(-1064.64, -43.26) * mm, v(-1055.9, -43.26) * mm, v(-1046.79, -43.26) * mm, v(-1037.14, -43.26) * mm, v(-1028.55, -43.26) * mm, v(-1021.28, -43.26) * mm, v(-1015.6, -43.26) * mm, v(-1009.73, -43.26) * mm, v(-1001.71, -43.26) * mm, v(-991.47, -43.26) * mm, v(-979.23, -43.26) * mm, v(-967.42, -43.26) * mm, v(-956.46, -43.26) * mm, v(-948.37, -43.26) * mm, v(-942.71, -43.26) * mm, v(-938.93, -43.26) * mm, v(-935.67, -43.26) * mm, v(-932.92, -43.26) * mm, v(-930.58, -43.26) * mm, v(-927.9, -43.26) * mm, v(-925.15, -43.26) * mm, v(-922.18, -43.26) * mm, v(-918.84, -43.26) * mm, v(-914.55, -43.26) * mm, v(-906.9, -43.26) * mm, v(-898.23, -43.26) * mm, v(-890.47, -43.26) * mm, v(-890.47, -43.26) * mm]});
            skLineSegment(sketch, "E185.0.0", {"start": v(-109.76, -43.26) * mm, "end": v(-109.76, -43.26) * mm});
            skFitSpline(sketch, "E185.0.1", {"points": [v(-890.47, -43.26) * mm, v(-896.1, -43.26) * mm, v(-905.56, -43.26) * mm, v(-915.53, -43.26) * mm, v(-922.39, -43.26) * mm, v(-926.45, -43.26) * mm, v(-929.27, -43.26) * mm, v(-931.32, -43.26) * mm, v(-933.43, -43.26) * mm, v(-935.75, -43.26) * mm, v(-938.24, -43.26) * mm, v(-941.76, -43.26) * mm, v(-946.45, -43.26) * mm, v(-951.34, -43.26) * mm, v(-955.27, -43.26) * mm, v(-958.2, -43.26) * mm, v(-961.08, -43.26) * mm, v(-964.99, -43.26) * mm, v(-970.12, -43.26) * mm, v(-977.21, -43.26) * mm, v(-984.33, -43.26) * mm, v(-991, -43.26) * mm, v(-996.58, -43.26) * mm, v(-1002.76, -43.26) * mm, v(-1009.65, -43.26) * mm, v(-1017.15, -43.26) * mm, v(-1027.88, -43.26) * mm, v(-1042.46, -43.26) * mm, v(-1061.2, -43.26) * mm, v(-1087.01, -43.26) * mm, v(-1112.84, -43.26) * mm, v(-1136.2, -43.26) * mm, v(-1151.88, -43.26) * mm, v(-1165.08, -43.26) * mm, v(-1173.51, -43.26) * mm, v(-1178.4, -43.26) * mm, v(-1181.05, -43.26) * mm, v(-1182.65, -43.26) * mm, v(-1183.5, -43.26) * mm, v(-1182.33, -43.26) * mm, v(-1177.99, -43.26) * mm, v(-1171.32, -43.26) * mm, v(-1162.96, -43.26) * mm, v(-1155.1, -43.26) * mm, v(-1148.57, -43.26) * mm, v(-1143.63, -43.26) * mm, v(-1138.74, -43.26) * mm, v(-1133.95, -43.26) * mm, v(-1129.25, -43.26) * mm, v(-1123.1, -43.26) * mm, v(-1115.6, -43.26) * mm, v(-1103.94, -43.26) * mm, v(-1092.64, -43.26) * mm, v(-1081.48, -43.26) * mm, v(-1073.11, -43.26) * mm, v(-1064.64, -43.26) * mm, v(-1055.9, -43.26) * mm, v(-1046.79, -43.26) * mm, v(-1037.14, -43.26) * mm, v(-1028.55, -43.26) * mm, v(-1021.28, -43.26) * mm, v(-1015.6, -43.26) * mm, v(-1009.73, -43.26) * mm, v(-1001.71, -43.26) * mm, v(-991.47, -43.26) * mm, v(-979.23, -43.26) * mm, v(-967.42, -43.26) * mm, v(-956.46, -43.26) * mm, v(-948.37, -43.26) * mm, v(-942.71, -43.26) * mm, v(-938.93, -43.26) * mm, v(-935.67, -43.26) * mm, v(-932.92, -43.26) * mm, v(-930.58, -43.26) * mm, v(-927.9, -43.26) * mm, v(-925.15, -43.26) * mm, v(-922.18, -43.26) * mm, v(-918.84, -43.26) * mm, v(-914.55, -43.26) * mm, v(-906.9, -43.26) * mm, v(-898.23, -43.26) * mm, v(-890.47, -43.26) * mm, v(-890.47, -43.26) * mm]});
            skLineSegment(sketch, "E186", {"start": v(-799.54, 0) * mm, "end": v(-568.33, 0) * mm});
            skLineSegment(sketch, "E187", {"start": v(-546.97, -12) * mm, "end": v(-799.54, -12) * mm});
            skLineSegment(sketch, "E188", {"start": v(-799.54, -12) * mm, "end": v(-799.54, 0) * mm});
            skArc(sketch, "E189", {"start": v(-546.97, -12) * mm, "mid": v(-534.73, 34.8) * mm, "end": v(-568.33, 0) * mm});
            skLineSegment(sketch, "E190.0", {"start": v(-514.65, -25) * mm, "end": v(-66.51, -25) * mm});
            skSolve(sketch);
        }
        {
            var Q0;
            Q0 = qSketchRegion(id + "F20", true);
            extrude(context, id + "F21", {"entities" : qUnion([Q0]), "operationType" : NewBodyOperationType.REMOVE, "endBound" : BoundingType.SYMMETRIC, "oppositeDirection" : true, "depth" : 200 * mm});
        }
    });
